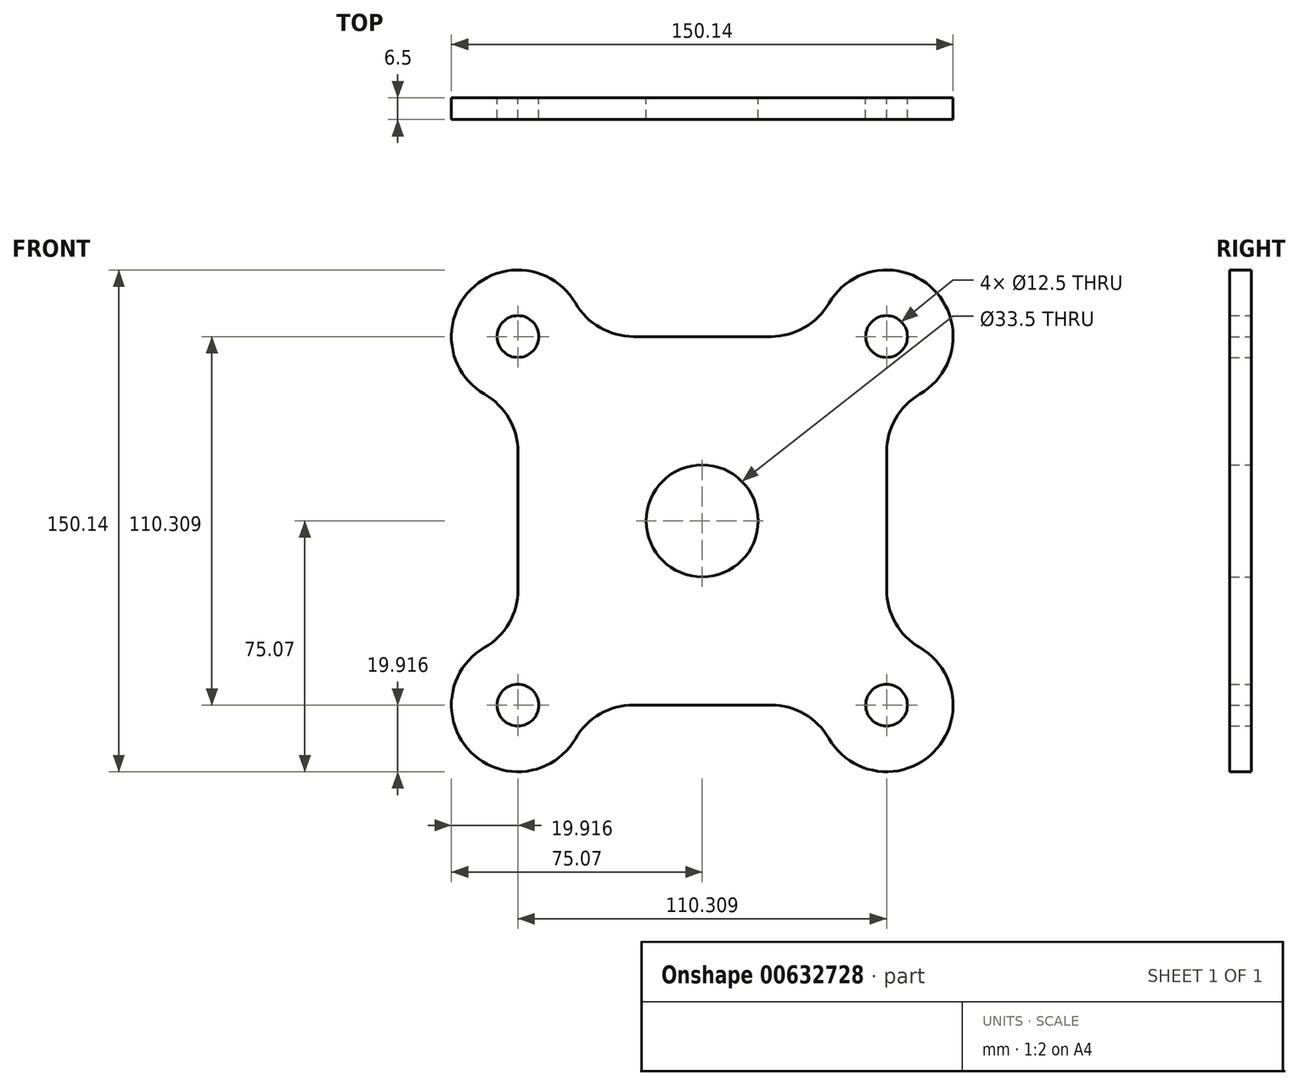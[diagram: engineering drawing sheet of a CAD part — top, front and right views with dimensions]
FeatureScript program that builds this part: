
annotation { "Feature Type Name" : "Feature", "Feature Type Description" : "" }
export const myFeature = defineFeature(function(context is Context, id is Id, definition is map)
    precondition{}
    {
        {
            var Q0;
            Q0=qCreatedBy(makeId("Front.planeOp"),FACE);
            var sketch = newSketch(context, id + "F0", { "sketchPlane" : qUnion([Q0])});
            skCircle(sketch, "E0", {"center": v(0, 0) * mm, "radius": 16.75 * mm});
            skCircle(sketch, "E1", {"center": v(-55.15, 55.15) * mm, "radius": 6.25 * mm});
            skPoint(sketch, "E2.endSnap0", {"position": v(-55.15, 0) * mm});
            skArc(sketch, "E3", {"start": v(-37.91, 65.13) * mm, "mid": v(-69.24, 69.24) * mm, "end": v(-65.13, 37.91) * mm});
            skLineSegment(sketch, "E4", {"start": v(-55.15, 20.6) * mm, "end": v(-55.15, 0) * mm});
            skLineSegment(sketch, "E5", {"start": v(-20.6, 55.15) * mm, "end": v(0, 55.15) * mm});
            skPoint(sketch, "E6.visualSharp", {"position": v(-35.23, 55.15) * mm});
            skArc(sketch, "E6.filletArc", {"start": v(-37.91, 65.13) * mm, "mid": v(-30.6, 57.83) * mm, "end": v(-20.6, 55.15) * mm});
            skPoint(sketch, "E7.visualSharp", {"position": v(-55.15, 35.23) * mm});
            skArc(sketch, "E7.filletArc", {"start": v(-55.15, 20.6) * mm, "mid": v(-57.83, 30.6) * mm, "end": v(-65.13, 37.91) * mm});
            skLineSegment(sketch, "E8.1.0", {"start": v(-55.15, -20.6) * mm, "end": v(-55.15, 0) * mm});
            skArc(sketch, "E8.1.1", {"start": v(-65.13, -37.91) * mm, "mid": v(-57.83, -30.6) * mm, "end": v(-55.15, -20.6) * mm});
            skArc(sketch, "E8.1.2", {"start": v(-65.13, -37.91) * mm, "mid": v(-69.24, -69.24) * mm, "end": v(-37.91, -65.13) * mm});
            skCircle(sketch, "E8.1.3", {"center": v(-55.15, -55.15) * mm, "radius": 6.25 * mm});
            skArc(sketch, "E8.1.4", {"start": v(-20.6, -55.15) * mm, "mid": v(-30.6, -57.83) * mm, "end": v(-37.91, -65.13) * mm});
            skLineSegment(sketch, "E8.1.5", {"start": v(-20.6, -55.15) * mm, "end": v(0, -55.15) * mm});
            skLineSegment(sketch, "E8.2.0", {"start": v(20.6, -55.15) * mm, "end": v(0, -55.15) * mm});
            skArc(sketch, "E8.2.1", {"start": v(37.91, -65.13) * mm, "mid": v(30.6, -57.83) * mm, "end": v(20.6, -55.15) * mm});
            skArc(sketch, "E8.2.2", {"start": v(37.91, -65.13) * mm, "mid": v(69.24, -69.24) * mm, "end": v(65.13, -37.91) * mm});
            skCircle(sketch, "E8.2.3", {"center": v(55.15, -55.15) * mm, "radius": 6.25 * mm});
            skArc(sketch, "E8.2.4", {"start": v(55.15, -20.6) * mm, "mid": v(57.83, -30.6) * mm, "end": v(65.13, -37.91) * mm});
            skLineSegment(sketch, "E8.2.5", {"start": v(55.15, -20.6) * mm, "end": v(55.15, 0) * mm});
            skLineSegment(sketch, "E8.3.0", {"start": v(55.15, 20.6) * mm, "end": v(55.15, 0) * mm});
            skArc(sketch, "E8.3.1", {"start": v(65.13, 37.91) * mm, "mid": v(57.83, 30.6) * mm, "end": v(55.15, 20.6) * mm});
            skArc(sketch, "E8.3.2", {"start": v(65.13, 37.91) * mm, "mid": v(69.24, 69.24) * mm, "end": v(37.91, 65.13) * mm});
            skCircle(sketch, "E8.3.3", {"center": v(55.15, 55.15) * mm, "radius": 6.25 * mm});
            skArc(sketch, "E8.3.4", {"start": v(20.6, 55.15) * mm, "mid": v(30.6, 57.83) * mm, "end": v(37.91, 65.13) * mm});
            skLineSegment(sketch, "E8.3.5", {"start": v(20.6, 55.15) * mm, "end": v(0, 55.15) * mm});
            skSolve(sketch);
        }
        {
            var Q0;
            Q0 = qSketchRegion(id + "F0", true);
            extrude(context, id + "F1", {"entities" : qUnion([Q0]), "depth" : 6.5 * mm, "offsetDistance" : 25 * mm});
        }
    });
